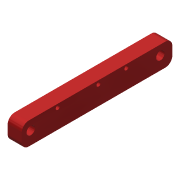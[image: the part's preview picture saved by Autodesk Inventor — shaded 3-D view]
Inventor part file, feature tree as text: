
AUTODESK INVENTOR PART (.ipt)
format: ipt  version: 2019.4 (Build 234330000, 330)  size: 114,176 bytes
history: native  units: mm
features: reference x6, other x5, extrude x1, sketch x1
ambient origin geometry x8: Origin, YZ Plane, XZ Plane, XY Plane, X Axis, Y Axis, Z Axis, Center Point
bodies: Solid1 (feature_tree)
feature tree (13):
  extrude  "Extrusion1"  Depth=5.0mm
  sketch  "Sketch1"  dims[d0=16.0mm d1=5.0mm d2=2.9mm d3=2.9mm d4=10.0mm d5=0.0mm]
  reference  "Reference1"
  reference  "Reference2"
  reference  "Reference3"
  reference  "Reference4"
  reference  "Reference5"
  reference  "Reference6"
  other  "Assembly_neje_slide_y_wellplateholder_20mmrod.iam"
  other  "00_Thorlabs_Rod_6mm:1"
  other  "00_Thorlabs_Rod_6mm:2"
  other  "Assembly_neje_slide_plate.iam"
  other  "Neje_Base_Slide_y_20mmrod_R11:1"
